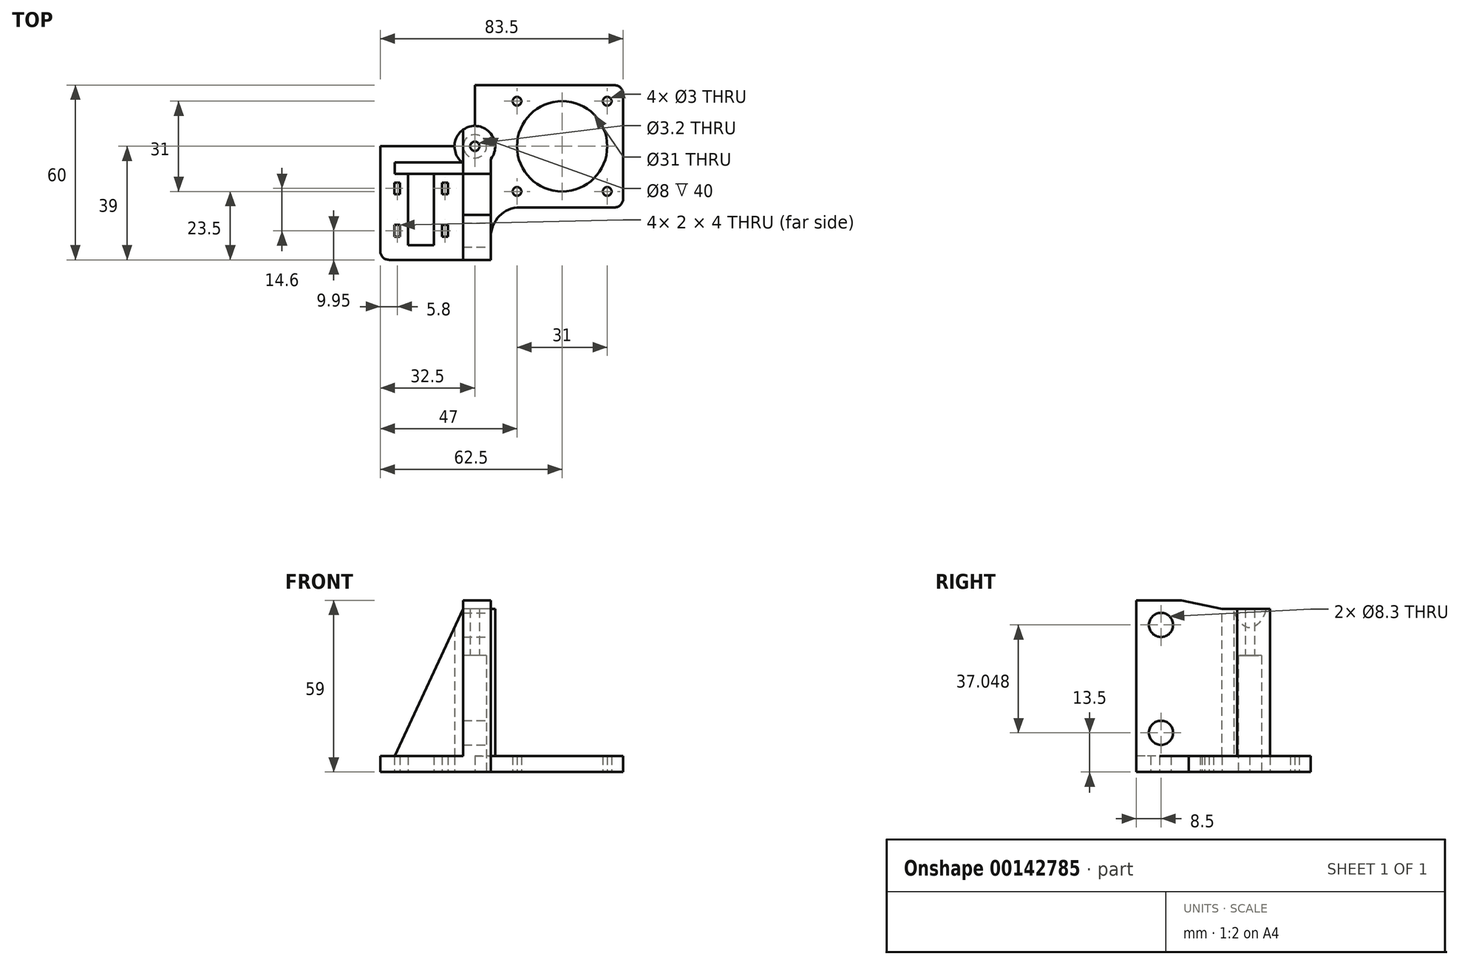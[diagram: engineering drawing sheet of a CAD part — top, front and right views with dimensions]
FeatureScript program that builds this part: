
annotation { "Feature Type Name" : "Feature", "Feature Type Description" : "" }
export const myFeature = defineFeature(function(context is Context, id is Id, definition is map)
    precondition{}
    {
        {
            var Q0;
            Q0=qCreatedBy(makeId("Top.planeOp"),FACE);
            var sketch = newSketch(context, id + "F0", { "sketchPlane" : qUnion([Q0])});
            skCircle(sketch, "E0", {"center": v(30, 0) * mm, "radius": 15.5 * mm});
            skLineSegment(sketch, "E1.bottom", {"start": v(14.5, 15.5) * mm, "end": v(45.5, 15.5) * mm, "construction": true});
            skLineSegment(sketch, "E1.top", {"start": v(14.5, -15.5) * mm, "end": v(45.5, -15.5) * mm, "construction": true});
            skLineSegment(sketch, "E1.left", {"start": v(14.5, 15.5) * mm, "end": v(14.5, -15.5) * mm, "construction": true});
            skLineSegment(sketch, "E1.right", {"start": v(45.5, 15.5) * mm, "end": v(45.5, -15.5) * mm, "construction": true});
            skCircle(sketch, "E2", {"center": v(14.5, 15.5) * mm, "radius": 1.5 * mm});
            skCircle(sketch, "E3", {"center": v(45.5, 15.5) * mm, "radius": 1.5 * mm});
            skCircle(sketch, "E4", {"center": v(14.5, -15.5) * mm, "radius": 1.5 * mm});
            skCircle(sketch, "E5", {"center": v(45.5, -15.5) * mm, "radius": 1.5 * mm});
            skLineSegment(sketch, "E6.bottom", {"start": v(0, 21) * mm, "end": v(51, 21) * mm});
            skLineSegment(sketch, "E6.top", {"start": v(0, -21) * mm, "end": v(51, -21) * mm});
            skLineSegment(sketch, "E6.left", {"start": v(0, 21) * mm, "end": v(0, -21) * mm});
            skLineSegment(sketch, "E6.right", {"start": v(51, 21) * mm, "end": v(51, -21) * mm});
            skLineSegment(sketch, "E7", {"start": v(45.5, 15.5) * mm, "end": v(45.5, 21) * mm, "construction": true});
            skLineSegment(sketch, "E8", {"start": v(45.5, 15.5) * mm, "end": v(51, 15.5) * mm, "construction": true});
            skSolve(sketch);
        }
        {
            var Q0;
            Q0=qCreatedBy(makeId("Top.planeOp"),FACE);
            var sketch = newSketch(context, id + "F1", { "sketchPlane" : qUnion([Q0])});
            skLineSegment(sketch, "E9.bottom", {"start": v(-32.5, 0) * mm, "end": v(0, 0) * mm});
            skLineSegment(sketch, "E9.top", {"start": v(-32.5, -39) * mm, "end": v(0, -39) * mm});
            skLineSegment(sketch, "E9.left", {"start": v(-32.5, 0) * mm, "end": v(-32.5, -39) * mm});
            skLineSegment(sketch, "E9.right", {"start": v(0, 0) * mm, "end": v(0, -39) * mm});
            skLineSegment(sketch, "E10.bottom", {"start": v(-23, -9.5) * mm, "end": v(-14, -9.5) * mm});
            skLineSegment(sketch, "E10.top", {"start": v(-23, -34) * mm, "end": v(-14, -34) * mm});
            skLineSegment(sketch, "E10.left", {"start": v(-23, -9.5) * mm, "end": v(-23, -34) * mm});
            skLineSegment(sketch, "E10.right", {"start": v(-14, -9.5) * mm, "end": v(-14, -34) * mm});
            skLineSegment(sketch, "E11", {"start": v(-18.5, -9.5) * mm, "end": v(-18.5, -34) * mm, "construction": true});
            skLineSegment(sketch, "E12", {"start": v(-23, -21.75) * mm, "end": v(-14, -21.75) * mm, "construction": true});
            skLineSegment(sketch, "E13.bottom", {"start": v(-27.7, -12.45) * mm, "end": v(-25.7, -12.45) * mm});
            skLineSegment(sketch, "E13.top", {"start": v(-27.7, -16.45) * mm, "end": v(-25.7, -16.45) * mm});
            skLineSegment(sketch, "E13.left", {"start": v(-27.7, -12.45) * mm, "end": v(-27.7, -16.45) * mm});
            skLineSegment(sketch, "E13.right", {"start": v(-25.7, -12.45) * mm, "end": v(-25.7, -16.45) * mm});
            skLineSegment(sketch, "E14", {"start": v(-26.7, -12.45) * mm, "end": v(-26.7, -16.45) * mm, "construction": true});
            skLineSegment(sketch, "E15", {"start": v(-27.7, -14.45) * mm, "end": v(-25.7, -14.45) * mm, "construction": true});
            skLineSegment(sketch, "E16.MirrorCS", {"start": v(-9.3, -12.45) * mm, "end": v(-11.3, -12.45) * mm});
            skLineSegment(sketch, "E17.MirrorCS", {"start": v(-11.3, -12.45) * mm, "end": v(-11.3, -16.45) * mm});
            skLineSegment(sketch, "E18.MirrorCS", {"start": v(-9.3, -12.45) * mm, "end": v(-9.3, -16.45) * mm});
            skLineSegment(sketch, "E19.MirrorCS", {"start": v(-9.3, -16.45) * mm, "end": v(-11.3, -16.45) * mm});
            skLineSegment(sketch, "E20.MirrorCS", {"start": v(-9.3, -31.05) * mm, "end": v(-11.3, -31.05) * mm});
            skLineSegment(sketch, "E21.MirrorCS", {"start": v(-9.3, -31.05) * mm, "end": v(-9.3, -27.05) * mm});
            skLineSegment(sketch, "E22.MirrorCS", {"start": v(-9.3, -27.05) * mm, "end": v(-11.3, -27.05) * mm});
            skLineSegment(sketch, "E23.MirrorCS", {"start": v(-11.3, -31.05) * mm, "end": v(-11.3, -27.05) * mm});
            skLineSegment(sketch, "E24.MirrorCS", {"start": v(-25.7, -31.05) * mm, "end": v(-25.7, -27.05) * mm});
            skLineSegment(sketch, "E25.MirrorCS", {"start": v(-27.7, -27.05) * mm, "end": v(-25.7, -27.05) * mm});
            skLineSegment(sketch, "E26.MirrorCS", {"start": v(-27.7, -31.05) * mm, "end": v(-25.7, -31.05) * mm});
            skLineSegment(sketch, "E27.MirrorCS", {"start": v(-27.7, -31.05) * mm, "end": v(-27.7, -27.05) * mm});
            skSolve(sketch);
        }
        {
            var Q0;
            Q0=qCreatedBy(makeId("Top.planeOp"),FACE);
            var sketch = newSketch(context, id + "F2", { "sketchPlane" : qUnion([Q0])});
            skCircle(sketch, "E28", {"center": v(0, 0) * mm, "radius": 7 * mm});
            skCircle(sketch, "E29", {"center": v(0, 0) * mm, "radius": 1.6 * mm});
            skLineSegment(sketch, "E30.bottom", {"start": v(-4, 0) * mm, "end": v(5.5, 0) * mm});
            skLineSegment(sketch, "E30.top", {"start": v(-4, -39) * mm, "end": v(5.5, -39) * mm});
            skLineSegment(sketch, "E30.left", {"start": v(-4, 0) * mm, "end": v(-4, -39) * mm});
            skLineSegment(sketch, "E30.right", {"start": v(5.5, 0) * mm, "end": v(5.5, -39) * mm});
            skCircle(sketch, "E31", {"center": v(0, 0) * mm, "radius": 4 * mm});
            skSolve(sketch);
        }
        {
            var Q0;
            Q0=qCreatedBy(makeId("Top.planeOp"),FACE);
            var sketch = newSketch(context, id + "F3", { "sketchPlane" : qUnion([Q0])});
            skLineSegment(sketch, "E32.bottom", {"start": v(-27.5, -5.5) * mm, "end": v(0, -5.5) * mm});
            skLineSegment(sketch, "E32.top", {"start": v(-27.5, -9.5) * mm, "end": v(0, -9.5) * mm});
            skLineSegment(sketch, "E32.left", {"start": v(-27.5, -5.5) * mm, "end": v(-27.5, -9.5) * mm});
            skLineSegment(sketch, "E32.right", {"start": v(0, -5.5) * mm, "end": v(0, -9.5) * mm});
            skSolve(sketch);
        }
        {
            var Q0;
            Q0=makeQuery(id+"F0.imprint","IMPRINT",FACE,{"disambiguationData":[TD([[makeQuery(id+"F0.imprint","IMPRINT",EDGE,{"derivedFrom":sQuery(id+"F0.wireOp",EDGE,"E0")}),-1.0]])]});
            extrude(context, id + "F4", {"entities" : qUnion([Q0]), "depth" : 5.5 * mm});
        }
        {
            var Q0;
            Q0=makeQuery(id+"F1.imprint","IMPRINT",FACE,{"disambiguationData":[TD([[makeQuery(id+"F1.imprint","IMPRINT",EDGE,{"derivedFrom":sQuery(id+"F1.wireOp",EDGE,"E9.bottom")}),-1.0]])]});
            var Q1;
            Q1=makeQuery(id+"F4.opExtrude","CAP_FACE",FACE,{"disambiguationData":[OSD([sQuery(id+"F0.wireOp",EDGE,"E0"),sQuery(id+"F0.wireOp",EDGE,"E2"),sQuery(id+"F0.wireOp",EDGE,"E3"),sQuery(id+"F0.wireOp",EDGE,"E4"),sQuery(id+"F0.wireOp",EDGE,"E5"),sQuery(id+"F0.wireOp",EDGE,"E6.bottom"),sQuery(id+"F0.wireOp",EDGE,"E6.top"),sQuery(id+"F0.wireOp",EDGE,"E6.left"),sQuery(id+"F0.wireOp",EDGE,"E6.right")])],"isStart":false});
            extrude(context, id + "F5", {"entities" : qUnion([Q0]), "operationType" : NewBodyOperationType.ADD, "endBound" : BoundingType.UP_TO_SURFACE, "endBoundEntityFace" : qUnion([Q1]), "depth" : 25 * mm});
        }
        {
            var Q0;
            {var subQ5=sQuery(id+"F2.wireOp",EDGE,"E30.top");Q0=makeQuery(id+"F2.imprint","IMPRINT",FACE,{"disambiguationData":[TD([[makeQuery(id+"F2.imprint","IMPRINT",EDGE,{"derivedFrom":subQ5}),1.0]])]});}
            var Q1;
            {var subQ3=sQuery(id+"F2.wireOp",EDGE,"E28");var subQ6=sQuery(id+"F2.wireOp",EDGE,"E30.left");var subQ8=makeQuery(id+"F2.imprint","INTERSECT",VERTEX,{"derivedFrom":[subQ3,subQ6]});Q1=makeQuery(id+"F2.imprint","IMPRINT",FACE,{"disambiguationData":[TD([[makeQuery(id+"F2.imprint","IMPRINT",EDGE,{"disambiguationData":[TD([[subQ8,-1.0]])],"derivedFrom":subQ3}),1.0]])]});}
            var Q2;
            {var subQ3=sQuery(id+"F2.wireOp",EDGE,"E28");var subQ5=sQuery(id+"F2.wireOp",EDGE,"E30.left");var subQ6=makeQuery(id+"F2.imprint","INTERSECT",VERTEX,{"derivedFrom":[subQ3,subQ5]});Q2=makeQuery(id+"F2.imprint","IMPRINT",FACE,{"disambiguationData":[TD([[makeQuery(id+"F2.imprint","IMPRINT",EDGE,{"disambiguationData":[TD([[subQ6,1.0]])],"derivedFrom":subQ3}),1.0]])]});}
            var Q3;
            {var subQ0=sQuery(id+"F2.wireOp",EDGE,"E30.bottom");var subQ1=sQuery(id+"F2.wireOp",EDGE,"E29");var subQ2=makeQuery(id+"F2.imprint","INTERSECT",VERTEX,{"disambiguationData":[OD(0.0)],"derivedFrom":[subQ1,subQ0]});Q3=makeQuery(id+"F2.imprint","IMPRINT",FACE,{"disambiguationData":[TD([[makeQuery(id+"F2.imprint","IMPRINT",EDGE,{"disambiguationData":[TD([[subQ2,1.0]])],"derivedFrom":subQ1}),-1.0]])]});}
            var Q4;
            {var subQ0=sQuery(id+"F2.wireOp",EDGE,"E30.bottom");var subQ1=sQuery(id+"F2.wireOp",EDGE,"E29");var subQ2=makeQuery(id+"F2.imprint","INTERSECT",VERTEX,{"disambiguationData":[OD(0.0)],"derivedFrom":[subQ1,subQ0]});Q4=makeQuery(id+"F2.imprint","IMPRINT",FACE,{"disambiguationData":[TD([[makeQuery(id+"F2.imprint","IMPRINT",EDGE,{"disambiguationData":[TD([[subQ2,-1.0]])],"derivedFrom":subQ1}),-1.0]])]});}
            var Q5;
            {var subQ0=sQuery(id+"F2.wireOp",EDGE,"E30.bottom");var subQ1=sQuery(id+"F2.wireOp",EDGE,"E29");var subQ2=makeQuery(id+"F2.imprint","INTERSECT",VERTEX,{"disambiguationData":[OD(0.0)],"derivedFrom":[subQ1,subQ0]});Q5=makeQuery(id+"F2.imprint","IMPRINT",FACE,{"disambiguationData":[TD([[makeQuery(id+"F2.imprint","IMPRINT",EDGE,{"disambiguationData":[TD([[subQ2,-1.0]])],"derivedFrom":subQ1}),1.0]])]});}
            var Q6;
            {var subQ0=sQuery(id+"F2.wireOp",EDGE,"E30.bottom");var subQ1=sQuery(id+"F2.wireOp",EDGE,"E29");var subQ2=makeQuery(id+"F2.imprint","INTERSECT",VERTEX,{"disambiguationData":[OD(0.0)],"derivedFrom":[subQ1,subQ0]});Q6=makeQuery(id+"F2.imprint","IMPRINT",FACE,{"disambiguationData":[TD([[makeQuery(id+"F2.imprint","IMPRINT",EDGE,{"disambiguationData":[TD([[subQ2,1.0]])],"derivedFrom":subQ1}),1.0]])]});}
            extrude(context, id + "F6", {"entities" : qUnion([Q0, Q1, Q2, Q3, Q4, Q5, Q6]), "operationType" : NewBodyOperationType.ADD, "depth" : 59 * mm});
        }
        {
            var Q0;
            Q0=makeQuery(id+"F3.imprint","IMPRINT",FACE,{"disambiguationData":[TD([[makeQuery(id+"F3.imprint","IMPRINT",EDGE,{"derivedFrom":sQuery(id+"F3.wireOp",EDGE,"E32.bottom")}),-1.0]])]});
            var Q1;
            Q1=makeQuery(id+"F6.opExtrude","CAP_FACE",FACE,{"disambiguationData":[OSD([sQuery(id+"F2.wireOp",EDGE,"E28"),sQuery(id+"F2.wireOp",EDGE,"E30.top"),sQuery(id+"F2.wireOp",EDGE,"E30.left"),sQuery(id+"F2.wireOp",EDGE,"E30.right")])],"isStart":false});
            extrude(context, id + "F7", {"entities" : qUnion([Q0]), "operationType" : NewBodyOperationType.ADD, "endBoundEntityFace" : qUnion([Q1]), "depth" : 56 * mm});
        }
        {
            var Q0;
            Q0=qCreatedBy(makeId("Right.planeOp"),FACE);
            var sketch = newSketch(context, id + "F8", { "sketchPlane" : qUnion([Q0])});
            skLineSegment(sketch, "E33.bottom", {"start": v(-30.5, 50.55) * mm, "end": v(30.5, 50.55) * mm, "construction": true});
            skLineSegment(sketch, "E33.top", {"start": v(-30.5, 13.5) * mm, "end": v(30.5, 13.5) * mm, "construction": true});
            skLineSegment(sketch, "E33.left", {"start": v(-30.5, 50.55) * mm, "end": v(-30.5, 13.5) * mm, "construction": true});
            skLineSegment(sketch, "E33.right", {"start": v(30.5, 50.55) * mm, "end": v(30.5, 13.5) * mm, "construction": true});
            skCircle(sketch, "E34", {"center": v(-30.5, 50.55) * mm, "radius": 4.15 * mm});
            skCircle(sketch, "E35", {"center": v(-30.5, 13.5) * mm, "radius": 4.15 * mm});
            skCircle(sketch, "E36", {"center": v(30.5, 13.5) * mm, "radius": 4.15 * mm});
            skCircle(sketch, "E37", {"center": v(30.5, 50.55) * mm, "radius": 4.15 * mm});
            skSolve(sketch);
        }
        {
            var Q0;
            Q0=makeQuery(id+"F8.imprint","IMPRINT",FACE,{"disambiguationData":[TD([[makeQuery(id+"F8.imprint","IMPRINT",EDGE,{"derivedFrom":sQuery(id+"F8.wireOp",EDGE,"E37")}),1.0]])]});
            var Q1;
            Q1=makeQuery(id+"F8.imprint","IMPRINT",FACE,{"disambiguationData":[TD([[makeQuery(id+"F8.imprint","IMPRINT",EDGE,{"derivedFrom":sQuery(id+"F8.wireOp",EDGE,"E36")}),1.0]])]});
            var Q2;
            Q2=makeQuery(id+"F8.imprint","IMPRINT",FACE,{"disambiguationData":[TD([[makeQuery(id+"F8.imprint","IMPRINT",EDGE,{"derivedFrom":sQuery(id+"F8.wireOp",EDGE,"E35")}),1.0]])]});
            var Q3;
            Q3=makeQuery(id+"F8.imprint","IMPRINT",FACE,{"disambiguationData":[TD([[makeQuery(id+"F8.imprint","IMPRINT",EDGE,{"derivedFrom":sQuery(id+"F8.wireOp",EDGE,"E34")}),1.0]])]});
            extrude(context, id + "F9", {"entities" : qUnion([Q0, Q1, Q2, Q3]), "operationType" : NewBodyOperationType.REMOVE, "oppositeDirection" : true, "depth" : 12 * mm, "symmetric" : true});
        }
        {
            var Q0;
            {var subQ0=sQuery(id+"F2.wireOp",EDGE,"E30.bottom");var subQ1=sQuery(id+"F2.wireOp",EDGE,"E29");var subQ2=makeQuery(id+"F2.imprint","INTERSECT",VERTEX,{"disambiguationData":[OD(0.0)],"derivedFrom":[subQ1,subQ0]});Q0=makeQuery(id+"F2.imprint","IMPRINT",FACE,{"disambiguationData":[TD([[makeQuery(id+"F2.imprint","IMPRINT",EDGE,{"disambiguationData":[TD([[subQ2,1.0]])],"derivedFrom":subQ1}),-1.0]])]});}
            var Q1;
            {var subQ0=sQuery(id+"F2.wireOp",EDGE,"E30.bottom");var subQ1=sQuery(id+"F2.wireOp",EDGE,"E29");var subQ2=makeQuery(id+"F2.imprint","INTERSECT",VERTEX,{"disambiguationData":[OD(0.0)],"derivedFrom":[subQ1,subQ0]});Q1=makeQuery(id+"F2.imprint","IMPRINT",FACE,{"disambiguationData":[TD([[makeQuery(id+"F2.imprint","IMPRINT",EDGE,{"disambiguationData":[TD([[subQ2,-1.0]])],"derivedFrom":subQ1}),-1.0]])]});}
            var Q2;
            {var subQ0=sQuery(id+"F2.wireOp",EDGE,"E30.bottom");var subQ1=sQuery(id+"F2.wireOp",EDGE,"E29");var subQ2=makeQuery(id+"F2.imprint","INTERSECT",VERTEX,{"disambiguationData":[OD(0.0)],"derivedFrom":[subQ1,subQ0]});Q2=makeQuery(id+"F2.imprint","IMPRINT",FACE,{"disambiguationData":[TD([[makeQuery(id+"F2.imprint","IMPRINT",EDGE,{"disambiguationData":[TD([[subQ2,-1.0]])],"derivedFrom":subQ1}),1.0]])]});}
            var Q3;
            {var subQ0=sQuery(id+"F2.wireOp",EDGE,"E30.bottom");var subQ1=sQuery(id+"F2.wireOp",EDGE,"E29");var subQ2=makeQuery(id+"F2.imprint","INTERSECT",VERTEX,{"disambiguationData":[OD(0.0)],"derivedFrom":[subQ1,subQ0]});Q3=makeQuery(id+"F2.imprint","IMPRINT",FACE,{"disambiguationData":[TD([[makeQuery(id+"F2.imprint","IMPRINT",EDGE,{"disambiguationData":[TD([[subQ2,1.0]])],"derivedFrom":subQ1}),1.0]])]});}
            extrude(context, id + "F10", {"entities" : qUnion([Q0, Q1, Q2, Q3]), "operationType" : NewBodyOperationType.REMOVE, "depth" : 40 * mm});
        }
        {
            var Q0;
            {var subQ0=sQuery(id+"F2.wireOp",EDGE,"E30.bottom");var subQ1=sQuery(id+"F2.wireOp",EDGE,"E29");var subQ2=makeQuery(id+"F2.imprint","INTERSECT",VERTEX,{"disambiguationData":[OD(0.0)],"derivedFrom":[subQ1,subQ0]});Q0=makeQuery(id+"F2.imprint","IMPRINT",FACE,{"disambiguationData":[TD([[makeQuery(id+"F2.imprint","IMPRINT",EDGE,{"disambiguationData":[TD([[subQ2,1.0]])],"derivedFrom":subQ1}),1.0]])]});}
            var Q1;
            {var subQ0=sQuery(id+"F2.wireOp",EDGE,"E30.bottom");var subQ1=sQuery(id+"F2.wireOp",EDGE,"E29");var subQ2=makeQuery(id+"F2.imprint","INTERSECT",VERTEX,{"disambiguationData":[OD(0.0)],"derivedFrom":[subQ1,subQ0]});Q1=makeQuery(id+"F2.imprint","IMPRINT",FACE,{"disambiguationData":[TD([[makeQuery(id+"F2.imprint","IMPRINT",EDGE,{"disambiguationData":[TD([[subQ2,-1.0]])],"derivedFrom":subQ1}),1.0]])]});}
            var Q2;
            {var subQ0=sQuery(id+"F2.wireOp",EDGE,"E30.right");var subQ1=sQuery(id+"F2.wireOp",EDGE,"E30.left");var subQ2=sQuery(id+"F2.wireOp",EDGE,"E30.top");var subQ3=sQuery(id+"F2.wireOp",EDGE,"E28");Q2=makeQuery(id+"FZiWaRTJdURsapg_1.1.F6.boolean.opBoolean","MERGE",FACE,{"derivedFrom":[makeQuery(id+"F6.opExtrude","CAP_FACE",FACE,{"disambiguationData":[OSD([subQ3,subQ2,subQ1,subQ0])],"isStart":false}),makeQuery(id+"FZiWaRTJdURsapg_1.1.F6.opExtrude","CAP_FACE",FACE,{"disambiguationData":[OSD([subQ3,subQ2,subQ1,subQ0])],"isStart":false})]});}
            extrude(context, id + "F11", {"entities" : qUnion([Q0, Q1]), "operationType" : NewBodyOperationType.REMOVE, "endBound" : BoundingType.UP_TO_SURFACE, "endBoundEntityFace" : qUnion([Q2]), "depth" : 25 * mm});
        }
        {
            var Q0;
            Q0=makeQuery(id+"FZiWaRTJdURsapg_1.1.F6.boolean.opBoolean","INTERSECT",EDGE,{"derivedFrom":[makeQuery(id+"F4.opExtrude","SWEPT_FACE",FACE,{"disambiguationData":[OSD([sQuery(id+"F0.wireOp",EDGE,"E6.bottom")])]}),makeQuery(id+"FZiWaRTJdURsapg_1.1.F6.opExtrude","SWEPT_FACE",FACE,{"disambiguationData":[OSD([sQuery(id+"F2.wireOp",EDGE,"E30.right")])]})]});
            var Q1;
            Q1=makeQuery(id+"F6.boolean.opBoolean","INTERSECT",EDGE,{"derivedFrom":[makeQuery(id+"F4.opExtrude","SWEPT_FACE",FACE,{"disambiguationData":[OSD([sQuery(id+"F0.wireOp",EDGE,"E6.top")])]}),makeQuery(id+"F6.opExtrude","SWEPT_FACE",FACE,{"disambiguationData":[OSD([sQuery(id+"F2.wireOp",EDGE,"E30.right")])]})]});
            fillet(context, id + "F12", {"entities" : qUnion([Q0, Q1]), "radius" : 10 * mm, "tangentPropagation" : true, "allowEdgeOverflow" : false});
        }
        {
            var Q0;
            Q0=makeQuery(id+"F4.opExtrude","SWEPT_EDGE",EDGE,{"disambiguationData":[OSD([sQuery(id+"F0.wireOp",EDGE,"E6.bottom"),sQuery(id+"F0.wireOp",EDGE,"E6.right")])]});
            var Q1;
            Q1=makeQuery(id+"F4.opExtrude","SWEPT_EDGE",EDGE,{"disambiguationData":[OSD([sQuery(id+"F0.wireOp",EDGE,"E6.top"),sQuery(id+"F0.wireOp",EDGE,"E6.right")])]});
            var Q2;
            Q2=makeQuery(id+"FZiWaRTJdURsapg_1.1.F5.opExtrude","SWEPT_EDGE",EDGE,{"disambiguationData":[OSD([sQuery(id+"F1.wireOp",EDGE,"E9.top"),sQuery(id+"F1.wireOp",EDGE,"E9.left")])]});
            var Q3;
            Q3=makeQuery(id+"F5.opExtrude","SWEPT_EDGE",EDGE,{"disambiguationData":[OSD([sQuery(id+"F1.wireOp",EDGE,"E9.top"),sQuery(id+"F1.wireOp",EDGE,"E9.left")])]});
            fillet(context, id + "F13", {"entities" : qUnion([Q0, Q1, Q2, Q3]), "radius" : 3 * mm, "tangentPropagation" : true, "allowEdgeOverflow" : false});
        }
        {
            var Q0;
            Q0=qCreatedBy(makeId("Right.planeOp"),FACE);
            var sketch = newSketch(context, id + "F14", { "sketchPlane" : qUnion([Q0])});
            skLineSegment(sketch, "E38", {"start": v(-23.5, 59) * mm, "end": v(-9.5, 56) * mm});
            skLineSegment(sketch, "E39", {"start": v(-9.5, 56) * mm, "end": v(9.5, 56) * mm});
            skLineSegment(sketch, "E40", {"start": v(9.5, 56) * mm, "end": v(23.5, 59) * mm});
            skLineSegment(sketch, "E41", {"start": v(23.5, 59) * mm, "end": v(-23.5, 59) * mm});
            skLineSegment(sketch, "E42", {"start": v(0, 56) * mm, "end": v(0, 59) * mm, "construction": true});
            skSolve(sketch);
        }
        {
            var Q0;
            Q0=makeQuery(id+"F14.imprint","IMPRINT",FACE,{"disambiguationData":[TD([[makeQuery(id+"F14.imprint","IMPRINT",EDGE,{"derivedFrom":sQuery(id+"F14.wireOp",EDGE,"E38")}),1.0]])]});
            extrude(context, id + "F15", {"entities" : qUnion([Q0]), "operationType" : NewBodyOperationType.REMOVE, "depth" : 21.14 * mm, "symmetric" : true});
        }
        {
            var Q0;
            Q0=makeQuery(id+"F7.opExtrude","CAP_EDGE",EDGE,{"disambiguationData":[OSD([sQuery(id+"F3.wireOp",EDGE,"E32.left")])],"isStart":false});
            var Q1;
            Q1=makeQuery(id+"FZiWaRTJdURsapg_1.1.F7.opExtrude","CAP_EDGE",EDGE,{"disambiguationData":[OSD([sQuery(id+"F3.wireOp",EDGE,"E32.left")])],"isStart":false});
            chamfer(context, id + "F16", {"entities" : qUnion([Q0, Q1]), "chamferType" : ChamferType.TWO_OFFSETS, "width1" : 23.5 * mm, "oppositeDirection" : false, "width2" : 50.5 * mm, "tangentPropagation" : true});
        }
    });
